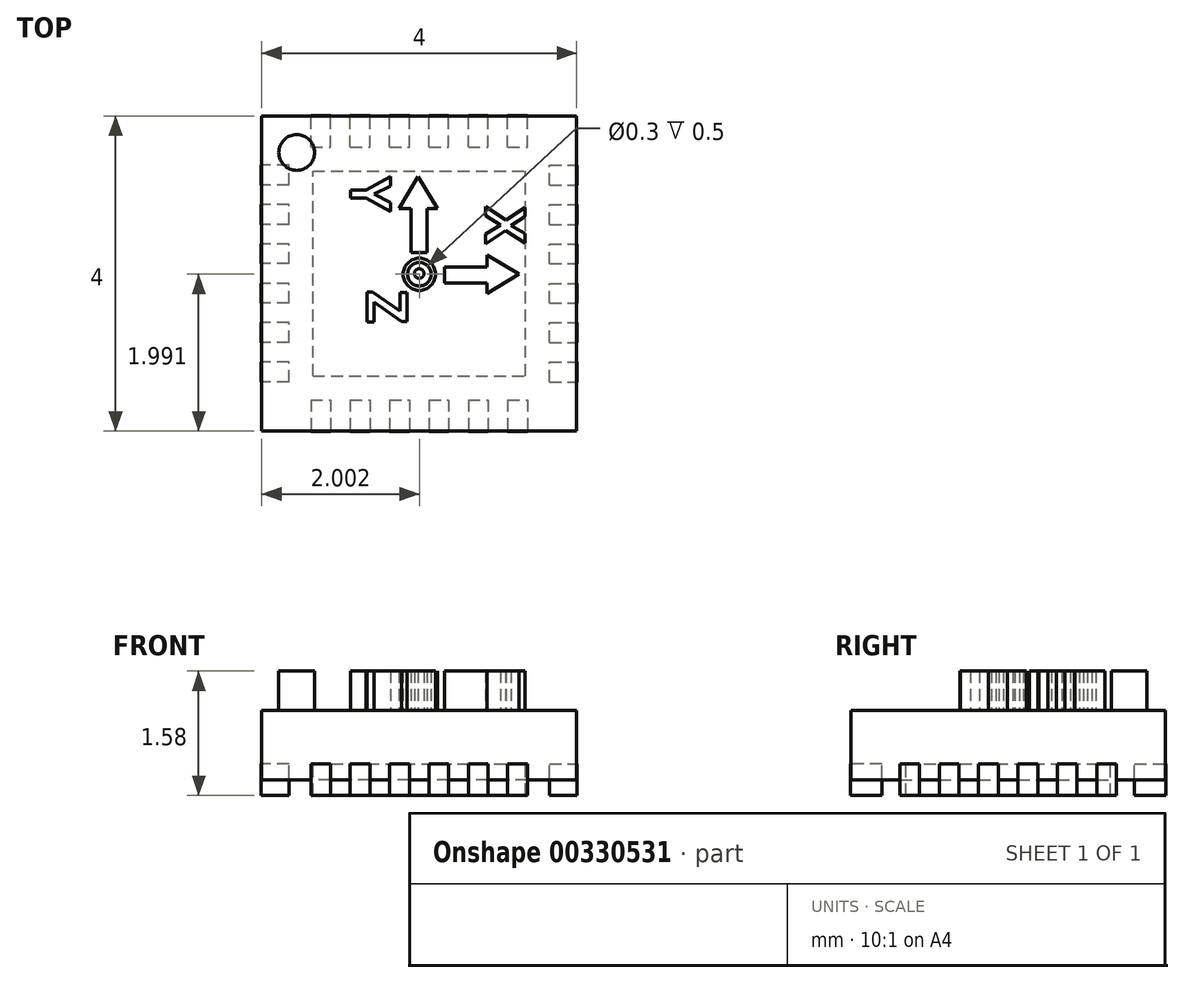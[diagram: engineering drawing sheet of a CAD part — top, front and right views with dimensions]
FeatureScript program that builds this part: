
annotation { "Feature Type Name" : "Feature", "Feature Type Description" : "" }
export const myFeature = defineFeature(function(context is Context, id is Id, definition is map)
    precondition{}
    {
        {
            var Q0;
            Q0=qCreatedBy(makeId("Top.planeOp"),FACE);
            var sketch = newSketch(context, id + "F0", { "sketchPlane" : qUnion([Q0])});
            skLineSegment(sketch, "E0.bottom", {"start": v(2, -2) * mm, "end": v(-2, -2) * mm});
            skLineSegment(sketch, "E0.top", {"start": v(2, 2) * mm, "end": v(-2, 2) * mm});
            skLineSegment(sketch, "E0.left", {"start": v(2, -2) * mm, "end": v(2, 2) * mm});
            skLineSegment(sketch, "E0.right", {"start": v(-2, -2) * mm, "end": v(-2, 2) * mm});
            skPoint(sketch, "E0.middle", {"position": v(0, 0) * mm});
            skSolve(sketch);
        }
        {
            var Q0;
            Q0 = qSketchRegion(id + "F0", true);
            extrude(context, id + "F1", {"entities" : qUnion([Q0]), "depth" : .88 * mm, "offsetDistance" : 25 * mm});
        }
        {
            var Q0;
            Q0=makeQuery(id+"F1.opExtrude","CAP_FACE",FACE,{"disambiguationData":[OSD([sQuery(id+"F0.wireOp",EDGE,"E0.bottom"),sQuery(id+"F0.wireOp",EDGE,"E0.top"),sQuery(id+"F0.wireOp",EDGE,"E0.left"),sQuery(id+"F0.wireOp",EDGE,"E0.right")])],"isStart":false});
            var sketch = newSketch(context, id + "F2", { "sketchPlane" : qUnion([Q0])});
            skCircle(sketch, "E1", {"center": v(-1.56, 1.54) * mm, "radius": 0.23 * mm});
            skSolve(sketch);
        }
        {
            var Q0;
            Q0 = qSketchRegion(id + "F2", true);
            extrude(context, id + "F3", {"entities" : qUnion([Q0]), "depth" : .5 * mm, "offsetDistance" : 25 * mm});
        }
        {
            var Q0;
            Q0=makeQuery(id+"F1.opExtrude","CAP_FACE",FACE,{"disambiguationData":[OSD([sQuery(id+"F0.wireOp",EDGE,"E0.bottom"),sQuery(id+"F0.wireOp",EDGE,"E0.top"),sQuery(id+"F0.wireOp",EDGE,"E0.left"),sQuery(id+"F0.wireOp",EDGE,"E0.right")])],"isStart":true});
            var sketch = newSketch(context, id + "F4", { "sketchPlane" : qUnion([Q0])});
            skLineSegment(sketch, "E2.bottom", {"start": v(1.66, -1.12) * mm, "end": v(2, -1.12) * mm});
            skLineSegment(sketch, "E2.top", {"start": v(1.66, -1.38) * mm, "end": v(2, -1.38) * mm});
            skLineSegment(sketch, "E2.left", {"start": v(1.66, -1.12) * mm, "end": v(1.66, -1.38) * mm});
            skLineSegment(sketch, "E2.right", {"start": v(2, -1.12) * mm, "end": v(2, -1.38) * mm});
            skPoint(sketch, "E2.middle", {"position": v(1.83, -1.25) * mm});
            skLineSegment(sketch, "E3", {"start": v(2, 0) * mm, "end": v(-2, 0) * mm, "construction": true});
            skLineSegment(sketch, "E4", {"start": v(0, -2) * mm, "end": v(0, 2) * mm, "construction": true});
            skLineSegment(sketch, "E5.0.1.0", {"start": v(1.66, -0.87) * mm, "end": v(2, -0.87) * mm});
            skLineSegment(sketch, "E5.0.1.1", {"start": v(1.66, -0.62) * mm, "end": v(1.66, -0.87) * mm});
            skLineSegment(sketch, "E5.0.1.2", {"start": v(2, -0.62) * mm, "end": v(2, -0.87) * mm});
            skLineSegment(sketch, "E5.0.1.3", {"start": v(1.66, -0.62) * mm, "end": v(2, -0.62) * mm});
            skPoint(sketch, "E5.0.1.4", {"position": v(1.83, -0.75) * mm});
            skLineSegment(sketch, "E5.0.2.0", {"start": v(1.66, -0.37) * mm, "end": v(2, -0.37) * mm});
            skLineSegment(sketch, "E5.0.2.1", {"start": v(1.66, -0.12) * mm, "end": v(1.66, -0.37) * mm});
            skLineSegment(sketch, "E5.0.2.2", {"start": v(2, -0.12) * mm, "end": v(2, -0.37) * mm});
            skLineSegment(sketch, "E5.0.2.3", {"start": v(1.66, -0.12) * mm, "end": v(2, -0.12) * mm});
            skPoint(sketch, "E5.0.2.4", {"position": v(1.83, -0.25) * mm});
            skLineSegment(sketch, "E5.0.3.0", {"start": v(1.66, 0.13) * mm, "end": v(2, 0.13) * mm});
            skLineSegment(sketch, "E5.0.3.1", {"start": v(1.66, 0.38) * mm, "end": v(1.66, 0.13) * mm});
            skLineSegment(sketch, "E5.0.3.2", {"start": v(2, 0.38) * mm, "end": v(2, 0.13) * mm});
            skLineSegment(sketch, "E5.0.3.3", {"start": v(1.66, 0.38) * mm, "end": v(2, 0.38) * mm});
            skPoint(sketch, "E5.0.3.4", {"position": v(1.83, 0.25) * mm});
            skLineSegment(sketch, "E5.0.4.0", {"start": v(1.66, 0.63) * mm, "end": v(2, 0.63) * mm});
            skLineSegment(sketch, "E5.0.4.1", {"start": v(1.66, 0.88) * mm, "end": v(1.66, 0.63) * mm});
            skLineSegment(sketch, "E5.0.4.2", {"start": v(2, 0.88) * mm, "end": v(2, 0.63) * mm});
            skLineSegment(sketch, "E5.0.4.3", {"start": v(1.66, 0.88) * mm, "end": v(2, 0.88) * mm});
            skPoint(sketch, "E5.0.4.4", {"position": v(1.83, 0.75) * mm});
            skLineSegment(sketch, "E5.0.5.0", {"start": v(1.66, 1.13) * mm, "end": v(2, 1.13) * mm});
            skLineSegment(sketch, "E5.0.5.1", {"start": v(1.66, 1.38) * mm, "end": v(1.66, 1.13) * mm});
            skLineSegment(sketch, "E5.0.5.2", {"start": v(2, 1.38) * mm, "end": v(2, 1.13) * mm});
            skLineSegment(sketch, "E5.0.5.3", {"start": v(1.66, 1.38) * mm, "end": v(2, 1.38) * mm});
            skPoint(sketch, "E5.0.5.4", {"position": v(1.83, 1.25) * mm});
            skLineSegment(sketch, "E5.direction1", {"start": v(1.66, -1.38) * mm, "end": v(2.16, -1.38) * mm, "construction": true});
            skLineSegment(sketch, "E5.direction2", {"start": v(1.66, -1.38) * mm, "end": v(1.66, -0.87) * mm, "construction": true});
            skLineSegment(sketch, "E6.MirrorCS", {"start": v(-1.66, -1.12) * mm, "end": v(-1.66, -1.38) * mm});
            skLineSegment(sketch, "E7.MirrorCS", {"start": v(-1.66, 1.38) * mm, "end": v(-2, 1.38) * mm});
            skLineSegment(sketch, "E8.MirrorCS", {"start": v(-1.66, 1.12) * mm, "end": v(-2, 1.12) * mm});
            skPoint(sketch, "E9.MirrorP", {"position": v(-1.83, -0.75) * mm});
            skLineSegment(sketch, "E10.MirrorCS", {"start": v(-1.66, 0.62) * mm, "end": v(-2, 0.62) * mm});
            skPoint(sketch, "E11.MirrorP", {"position": v(-1.83, -0.25) * mm});
            skLineSegment(sketch, "E12.MirrorCS", {"start": v(-1.66, 0.88) * mm, "end": v(-1.66, 0.62) * mm});
            skPoint(sketch, "E13.MirrorP", {"position": v(-1.83, 1.25) * mm});
            skLineSegment(sketch, "E14.MirrorCS", {"start": v(-1.66, -0.12) * mm, "end": v(-2, -0.12) * mm});
            skLineSegment(sketch, "E15.MirrorCS", {"start": v(-1.66, 0.12) * mm, "end": v(-2, 0.12) * mm});
            skLineSegment(sketch, "E16.MirrorCS", {"start": v(-1.66, 0.38) * mm, "end": v(-1.66, 0.12) * mm});
            skLineSegment(sketch, "E17.MirrorCS", {"start": v(-1.66, -1.13) * mm, "end": v(-2, -1.13) * mm});
            skLineSegment(sketch, "E18.MirrorCS", {"start": v(-2, 0.38) * mm, "end": v(-2, 0.12) * mm});
            skLineSegment(sketch, "E19.MirrorCS", {"start": v(-1.66, -1.38) * mm, "end": v(-2, -1.38) * mm});
            skLineSegment(sketch, "E20.MirrorCS", {"start": v(-1.66, -1.38) * mm, "end": v(-1.66, -0.87) * mm, "construction": true});
            skLineSegment(sketch, "E21.MirrorCS", {"start": v(-2, -1.13) * mm, "end": v(-2, -1.38) * mm});
            skLineSegment(sketch, "E22.MirrorCS", {"start": v(-1.66, -0.88) * mm, "end": v(-2, -0.88) * mm});
            skLineSegment(sketch, "E23.MirrorCS", {"start": v(-1.66, 1.38) * mm, "end": v(-1.66, 1.13) * mm});
            skLineSegment(sketch, "E24.MirrorCS", {"start": v(-1.66, -0.62) * mm, "end": v(-1.66, -0.88) * mm});
            skLineSegment(sketch, "E25.MirrorCS", {"start": v(-2, -0.62) * mm, "end": v(-2, -0.88) * mm});
            skLineSegment(sketch, "E26.MirrorCS", {"start": v(-1.66, -0.62) * mm, "end": v(-2, -0.62) * mm});
            skLineSegment(sketch, "E27.MirrorCS", {"start": v(-1.66, -0.38) * mm, "end": v(-2, -0.38) * mm});
            skPoint(sketch, "E28.MirrorP", {"position": v(-1.83, 0.25) * mm});
            skLineSegment(sketch, "E29.MirrorCS", {"start": v(-2, 0.88) * mm, "end": v(-2, 0.62) * mm});
            skLineSegment(sketch, "E30.MirrorCS", {"start": v(-1.66, -0.12) * mm, "end": v(-1.66, -0.38) * mm});
            skLineSegment(sketch, "E31.MirrorCS", {"start": v(-2, -0.12) * mm, "end": v(-2, -0.38) * mm});
            skLineSegment(sketch, "E32.MirrorCS", {"start": v(-1.66, 0.38) * mm, "end": v(-2, 0.38) * mm});
            skPoint(sketch, "E33.MirrorP", {"position": v(-1.83, -1.25) * mm});
            skLineSegment(sketch, "E34.MirrorCS", {"start": v(-1.66, 0.88) * mm, "end": v(-2, 0.88) * mm});
            skPoint(sketch, "E35.MirrorP", {"position": v(-1.83, 0.75) * mm});
            skLineSegment(sketch, "E36.MirrorCS", {"start": v(-2, 1.38) * mm, "end": v(-2, 1.12) * mm});
            skLineSegment(sketch, "E37.bottom", {"start": v(1.13, -1.6) * mm, "end": v(1.38, -1.6) * mm});
            skLineSegment(sketch, "E37.top", {"start": v(1.13, -2) * mm, "end": v(1.38, -2) * mm});
            skLineSegment(sketch, "E37.left", {"start": v(1.13, -1.6) * mm, "end": v(1.13, -2) * mm});
            skLineSegment(sketch, "E37.right", {"start": v(1.38, -1.6) * mm, "end": v(1.38, -2) * mm});
            skPoint(sketch, "E37.middle", {"position": v(1.25, -1.8) * mm});
            skPoint(sketch, "E38.1.0.0", {"position": v(0.75, -1.8) * mm});
            skLineSegment(sketch, "E38.1.0.1", {"start": v(0.88, -1.6) * mm, "end": v(0.88, -2) * mm});
            skLineSegment(sketch, "E38.1.0.2", {"start": v(0.63, -1.6) * mm, "end": v(0.63, -2) * mm});
            skLineSegment(sketch, "E38.1.0.3", {"start": v(0.63, -2) * mm, "end": v(0.88, -2) * mm});
            skLineSegment(sketch, "E38.1.0.4", {"start": v(0.63, -1.6) * mm, "end": v(0.88, -1.6) * mm});
            skPoint(sketch, "E38.2.0.0", {"position": v(0.25, -1.8) * mm});
            skLineSegment(sketch, "E38.2.0.1", {"start": v(0.38, -1.6) * mm, "end": v(0.38, -2) * mm});
            skLineSegment(sketch, "E38.2.0.2", {"start": v(0.13, -1.6) * mm, "end": v(0.13, -2) * mm});
            skLineSegment(sketch, "E38.2.0.3", {"start": v(0.13, -2) * mm, "end": v(0.38, -2) * mm});
            skLineSegment(sketch, "E38.2.0.4", {"start": v(0.13, -1.6) * mm, "end": v(0.38, -1.6) * mm});
            skPoint(sketch, "E38.3.0.0", {"position": v(-0.25, -1.8) * mm});
            skLineSegment(sketch, "E38.3.0.1", {"start": v(-0.12, -1.6) * mm, "end": v(-0.12, -2) * mm});
            skLineSegment(sketch, "E38.3.0.2", {"start": v(-0.37, -1.6) * mm, "end": v(-0.37, -2) * mm});
            skLineSegment(sketch, "E38.3.0.3", {"start": v(-0.37, -2) * mm, "end": v(-0.12, -2) * mm});
            skLineSegment(sketch, "E38.3.0.4", {"start": v(-0.37, -1.6) * mm, "end": v(-0.12, -1.6) * mm});
            skPoint(sketch, "E38.4.0.0", {"position": v(-0.75, -1.8) * mm});
            skLineSegment(sketch, "E38.4.0.1", {"start": v(-0.62, -1.6) * mm, "end": v(-0.62, -2) * mm});
            skLineSegment(sketch, "E38.4.0.2", {"start": v(-0.87, -1.6) * mm, "end": v(-0.87, -2) * mm});
            skLineSegment(sketch, "E38.4.0.3", {"start": v(-0.87, -2) * mm, "end": v(-0.62, -2) * mm});
            skLineSegment(sketch, "E38.4.0.4", {"start": v(-0.87, -1.6) * mm, "end": v(-0.62, -1.6) * mm});
            skPoint(sketch, "E38.5.0.0", {"position": v(-1.25, -1.8) * mm});
            skLineSegment(sketch, "E38.5.0.1", {"start": v(-1.12, -1.6) * mm, "end": v(-1.12, -2) * mm});
            skLineSegment(sketch, "E38.5.0.2", {"start": v(-1.37, -1.6) * mm, "end": v(-1.37, -2) * mm});
            skLineSegment(sketch, "E38.5.0.3", {"start": v(-1.37, -2) * mm, "end": v(-1.12, -2) * mm});
            skLineSegment(sketch, "E38.5.0.4", {"start": v(-1.37, -1.6) * mm, "end": v(-1.12, -1.6) * mm});
            skLineSegment(sketch, "E38.direction1", {"start": v(1.13, -2) * mm, "end": v(0.63, -2) * mm, "construction": true});
            skLineSegment(sketch, "E39.MirrorCS", {"start": v(1.13, 1.6) * mm, "end": v(1.38, 1.6) * mm});
            skLineSegment(sketch, "E40.MirrorCS", {"start": v(0.63, 1.6) * mm, "end": v(0.88, 1.6) * mm});
            skLineSegment(sketch, "E41.MirrorCS", {"start": v(-1.37, 1.6) * mm, "end": v(-1.12, 1.6) * mm});
            skLineSegment(sketch, "E42.MirrorCS", {"start": v(-0.37, 1.6) * mm, "end": v(-0.12, 1.6) * mm});
            skLineSegment(sketch, "E43.MirrorCS", {"start": v(1.13, 2) * mm, "end": v(0.63, 2) * mm, "construction": true});
            skLineSegment(sketch, "E44.MirrorCS", {"start": v(0.63, 2) * mm, "end": v(0.88, 2) * mm});
            skLineSegment(sketch, "E45.MirrorCS", {"start": v(-1.37, 2) * mm, "end": v(-1.12, 2) * mm});
            skLineSegment(sketch, "E46.MirrorCS", {"start": v(-0.37, 2) * mm, "end": v(-0.12, 2) * mm});
            skLineSegment(sketch, "E47.MirrorCS", {"start": v(-0.87, 1.6) * mm, "end": v(-0.62, 1.6) * mm});
            skLineSegment(sketch, "E48.MirrorCS", {"start": v(-0.87, 2) * mm, "end": v(-0.62, 2) * mm});
            skLineSegment(sketch, "E49.MirrorCS", {"start": v(0.13, 1.6) * mm, "end": v(0.38, 1.6) * mm});
            skLineSegment(sketch, "E50.MirrorCS", {"start": v(0.13, 2) * mm, "end": v(0.38, 2) * mm});
            skLineSegment(sketch, "E51.MirrorCS", {"start": v(1.13, 2) * mm, "end": v(1.38, 2) * mm});
            skLineSegment(sketch, "E52.MirrorCS", {"start": v(0.13, 1.6) * mm, "end": v(0.13, 2) * mm});
            skLineSegment(sketch, "E53.MirrorCS", {"start": v(-0.62, 1.6) * mm, "end": v(-0.62, 2) * mm});
            skLineSegment(sketch, "E54.MirrorCS", {"start": v(0.38, 1.6) * mm, "end": v(0.38, 2) * mm});
            skLineSegment(sketch, "E55.MirrorCS", {"start": v(0.63, 1.6) * mm, "end": v(0.63, 2) * mm});
            skLineSegment(sketch, "E56.MirrorCS", {"start": v(-1.37, 1.6) * mm, "end": v(-1.37, 2) * mm});
            skLineSegment(sketch, "E57.MirrorCS", {"start": v(-0.37, 1.6) * mm, "end": v(-0.37, 2) * mm});
            skLineSegment(sketch, "E58.MirrorCS", {"start": v(1.38, 1.6) * mm, "end": v(1.38, 2) * mm});
            skLineSegment(sketch, "E59.MirrorCS", {"start": v(-0.12, 1.6) * mm, "end": v(-0.12, 2) * mm});
            skLineSegment(sketch, "E60.MirrorCS", {"start": v(1.13, 1.6) * mm, "end": v(1.13, 2) * mm});
            skLineSegment(sketch, "E61.MirrorCS", {"start": v(0.88, 1.6) * mm, "end": v(0.88, 2) * mm});
            skLineSegment(sketch, "E62.MirrorCS", {"start": v(-1.12, 1.6) * mm, "end": v(-1.12, 2) * mm});
            skLineSegment(sketch, "E63.MirrorCS", {"start": v(-0.87, 1.6) * mm, "end": v(-0.87, 2) * mm});
            skPoint(sketch, "E64.MirrorP", {"position": v(-0.75, 1.8) * mm});
            skPoint(sketch, "E65.MirrorP", {"position": v(-0.25, 1.8) * mm});
            skLineSegment(sketch, "E66.MirrorCS", {"start": v(0, 2) * mm, "end": v(0, -2) * mm, "construction": true});
            skPoint(sketch, "E67.MirrorP", {"position": v(-1.25, 1.8) * mm});
            skPoint(sketch, "E68.MirrorP", {"position": v(0.25, 1.8) * mm});
            skPoint(sketch, "E69.MirrorP", {"position": v(1.25, 1.8) * mm});
            skPoint(sketch, "E70.MirrorP", {"position": v(0.75, 1.8) * mm});
            skLineSegment(sketch, "E71.bottom", {"start": v(-1.35, 1.3) * mm, "end": v(1.35, 1.3) * mm});
            skLineSegment(sketch, "E71.top", {"start": v(-1.35, -1.3) * mm, "end": v(1.35, -1.3) * mm});
            skLineSegment(sketch, "E71.left", {"start": v(-1.35, 1.3) * mm, "end": v(-1.35, -1.3) * mm});
            skLineSegment(sketch, "E71.right", {"start": v(1.35, 1.3) * mm, "end": v(1.35, -1.3) * mm});
            skPoint(sketch, "E71.middle", {"position": v(0, 0) * mm});
            skSolve(sketch);
        }
        {
            var Q0;
            Q0 = qSketchRegion(id + "F4", true);
            extrude(context, id + "F5", {"entities" : qUnion([Q0]), "depth" : .2 * mm, "offsetDistance" : 25 * mm, "hasSecondDirection" : true, "secondDirectionOppositeDirection" : true, "secondDirectionDepth" : .2 * mm});
        }
        {
            var Q0;
            Q0=makeQuery(id+"F1.opExtrude","CAP_FACE",FACE,{"disambiguationData":[OSD([sQuery(id+"F0.wireOp",EDGE,"E0.bottom"),sQuery(id+"F0.wireOp",EDGE,"E0.top"),sQuery(id+"F0.wireOp",EDGE,"E0.left"),sQuery(id+"F0.wireOp",EDGE,"E0.right")])],"isStart":false});
            var sketch = newSketch(context, id + "F6", { "sketchPlane" : qUnion([Q0])});
            skLineSegment(sketch, "E72.bottom", {"start": v(0.32, -0.12) * mm, "end": v(0.86, -0.12) * mm});
            skLineSegment(sketch, "E72.top", {"start": v(0.32, 0.08) * mm, "end": v(0.86, 0.08) * mm});
            skLineSegment(sketch, "E72.left", {"start": v(0.32, -0.12) * mm, "end": v(0.32, 0.08) * mm});
            skLineSegment(sketch, "E73", {"start": v(0.86, -0.12) * mm, "end": v(0.86, -0.25) * mm});
            skLineSegment(sketch, "E74", {"start": v(0.86, -0.25) * mm, "end": v(1.27, 0) * mm});
            skLineSegment(sketch, "E75", {"start": v(1.27, 0) * mm, "end": v(0.86, 0.23) * mm});
            skLineSegment(sketch, "E76", {"start": v(0.86, 0.23) * mm, "end": v(0.86, 0.08) * mm});
            skText(sketch, "E77", { "text": "X", "fontName": "OpenSans-Bold.ttf"});
            skLineSegment(sketch, "E78.bottom", {"start": v(0.1, 0.27) * mm, "end": v(0.1, 0.83) * mm});
            skLineSegment(sketch, "E78.top", {"start": v(-0.1, 0.27) * mm, "end": v(-0.1, 0.83) * mm});
            skLineSegment(sketch, "E78.left", {"start": v(0.1, 0.27) * mm, "end": v(-0.1, 0.27) * mm});
            skLineSegment(sketch, "E79", {"start": v(0.1, 0.83) * mm, "end": v(0.23, 0.83) * mm});
            skLineSegment(sketch, "E80", {"start": v(0.23, 0.83) * mm, "end": v(-0.01, 1.23) * mm});
            skLineSegment(sketch, "E81", {"start": v(-0.01, 1.23) * mm, "end": v(-0.26, 0.83) * mm});
            skLineSegment(sketch, "E82", {"start": v(-0.26, 0.83) * mm, "end": v(-0.1, 0.83) * mm});
            skText(sketch, "E83", { "text": "Y", "fontName": "OpenSans-Bold.ttf"});
            skCircle(sketch, "E84", {"center": v(0, 0) * mm, "radius": 0.2 * mm});
            skCircle(sketch, "E85", {"center": v(0, 0) * mm, "radius": 0.15 * mm});
            skText(sketch, "E86", { "text": "Z\n", "fontName": "OpenSans-Bold.ttf"});
            const initialGuessF6  = {"E77": [0.00084, 0.00085, 0, -1, 0.00051], "E83": [-0.00087, 0.00123, 0, -1, 0.00051], "E86": [-0.00066, -0.00022, 0, -1, 0.00051]};
            skSetInitialGuess(sketch, initialGuessF6);
            skSolve(sketch);
        }
        {
            var Q0;
            Q0 = qSketchRegion(id + "F6", true);
            extrude(context, id + "F7", {"entities" : qUnion([Q0]), "depth" : .5 * mm, "offsetDistance" : 25 * mm});
        }
        {
            var Q0;
            Q0=makeQuery(id+"F1.opExtrude","CAP_FACE",FACE,{"disambiguationData":[OSD([sQuery(id+"F0.wireOp",EDGE,"E0.bottom"),sQuery(id+"F0.wireOp",EDGE,"E0.top"),sQuery(id+"F0.wireOp",EDGE,"E0.left"),sQuery(id+"F0.wireOp",EDGE,"E0.right")])],"isStart":false});
            var sketch = newSketch(context, id + "F8", { "sketchPlane" : qUnion([Q0])});
            skCircle(sketch, "E87", {"center": v(0, 0) * mm, "radius": 0.06 * mm});
            skSolve(sketch);
        }
        {
            var Q0;
            Q0 = qSketchRegion(id + "F8", true);
            extrude(context, id + "F9", {"entities" : qUnion([Q0]), "depth" : .5 * mm, "offsetDistance" : 25 * mm});
        }
    });
